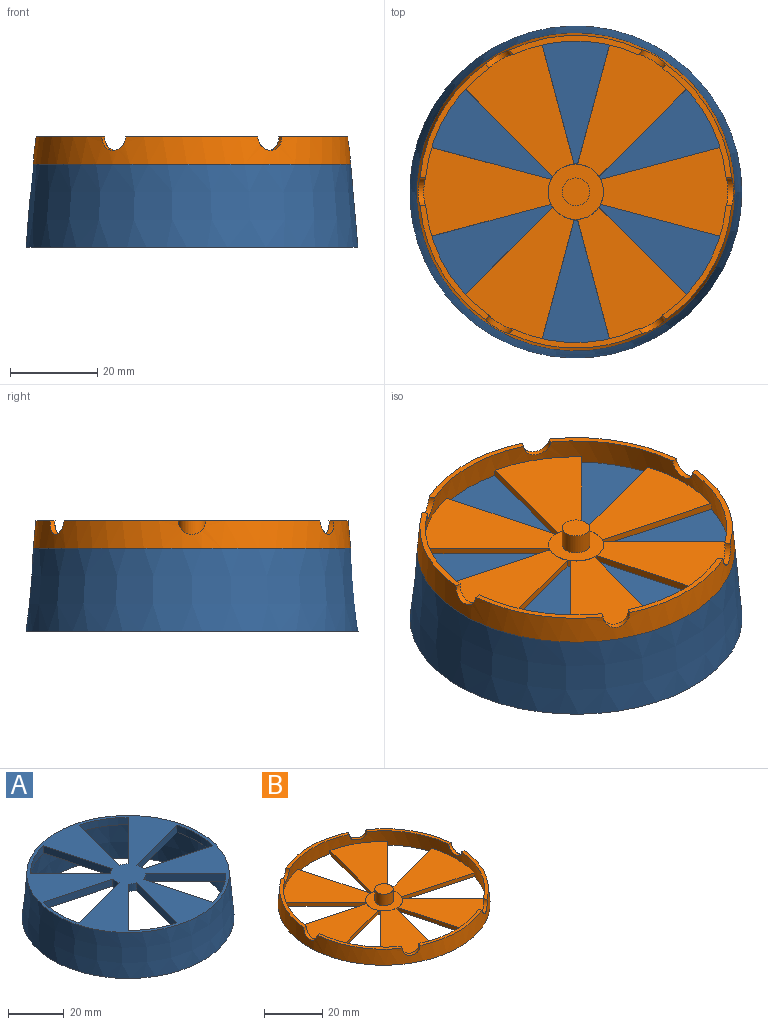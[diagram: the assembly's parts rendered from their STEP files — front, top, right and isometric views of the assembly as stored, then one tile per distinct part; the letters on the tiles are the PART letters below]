
ASSEMBLY  parts=2 mates=1
PART A: 29 faces, bbox 76.2x76.2x19.1 mm
  f0: cone r=38.1mm half-angle=5deg, axis (0,0,-1), area 4477.7mm2, adj f1,f4
  f1: plane 72.87x72.87mm, normal (0,0,1), area 2291.8mm2, adj f0,f5,f6,f7,f8,f9,f10,f11
  f2: plane 70.87x70.87mm, normal (0,0,-1), area 2066.6mm2, adj f3,f5,f6,f7,f8,f9,f10,f11
  f3: cone r=36.83mm half-angle=5deg, axis (0,0,-1), area 3617.6mm2, adj f2,f4
  f4: plane 76.2x76.2mm, normal (0,0,-1), area 300.1mm2, adj f0,f3
  f5: cylinder r=6.35mm len=3.29mm, axis (0,0,1), area 10.6mm2, adj f1,f2,f6,f8
  f6: plane 27.83x7.46mm, normal (-0.26,-0.97,0), area 91.5mm2, adj f1,f2,f5,f7
  f7: cylinder r=35.16mm len=18.2mm, axis (0,0,1), area 58.4mm2, adj f1,f2,f6,f8
  f8: plane 27.83x7.46mm, normal (-0.26,0.97,0), area 91.5mm2, adj f1,f2,f5,f7
  f9: cylinder r=6.35mm len=3.18mm, axis (0,0,1), area 10.6mm2, adj f1,f2,f10,f11
  f10: plane 20.37x20.37mm, normal (0.71,-0.71,0), area 91.5mm2, adj f1,f2,f9,f12
  f11: plane 27.83x7.46mm, normal (-0.97,0.26,0), area 91.5mm2, adj f1,f2,f9,f12
  f12: cylinder r=35.16mm len=15.76mm, axis (0,0,1), area 58.4mm2, adj f1,f2,f10,f11
  f13: cylinder r=6.35mm len=3.18mm, axis (0,0,1), area 10.6mm2, adj f1,f2,f14,f16
  f14: plane 27.83x7.46mm, normal (0.97,0.26,0), area 91.5mm2, adj f1,f2,f13,f15
  f15: cylinder r=35.16mm len=15.76mm, axis (0,0,1), area 58.4mm2, adj f1,f2,f14,f16
  f16: plane 20.37x20.37mm, normal (-0.71,-0.71,0), area 91.5mm2, adj f1,f2,f13,f15
  f17: cylinder r=6.35mm len=3.29mm, axis (0,0,1), area 10.6mm2, adj f1,f2,f18,f19
  f18: plane 27.83x7.46mm, normal (0.26,0.97,0), area 91.5mm2, adj f1,f2,f17,f20
  f19: plane 27.83x7.46mm, normal (0.26,-0.97,0), area 91.5mm2, adj f1,f2,f17,f20
  f20: cylinder r=35.16mm len=18.2mm, axis (0,0,1), area 58.4mm2, adj f1,f2,f18,f19
  f21: cylinder r=6.35mm len=3.18mm, axis (0,0,1), area 10.6mm2, adj f1,f2,f22,f23
  f22: plane 20.37x20.37mm, normal (-0.71,0.71,0), area 91.5mm2, adj f1,f2,f21,f24
  f23: plane 27.83x7.46mm, normal (0.97,-0.26,0), area 91.5mm2, adj f1,f2,f21,f24
  f24: cylinder r=35.16mm len=15.76mm, axis (0,0,1), area 58.4mm2, adj f1,f2,f22,f23
  f25: cylinder r=6.35mm len=3.18mm, axis (0,0,1), area 10.6mm2, adj f1,f2,f26,f27
  f26: plane 27.83x7.46mm, normal (-0.97,-0.26,0), area 91.5mm2, adj f1,f2,f25,f28
  f27: plane 20.37x20.37mm, normal (0.71,0.71,0), area 91.5mm2, adj f1,f2,f25,f28
  f28: cylinder r=35.16mm len=15.76mm, axis (0,0,1), area 58.4mm2, adj f1,f2,f26,f27
PART B: 43 faces, bbox 72.9x72.9x6.4 mm
  f0: cylinder r=3.17mm len=6.35mm, axis (0,0,1), area 95mm2, adj f8,f28
  f1: plane 30.63x25.26mm, normal (0,0,1), area 383.4mm2, adj f25,f26,f27,f42
  f2: plane 30.63x25.26mm, normal (0,0,1), area 383.4mm2, adj f22,f23,f24,f42
  f3: plane 29.34x20.57mm, normal (0,0,1), area 383.4mm2, adj f19,f20,f21,f42
  f4: plane 30.63x25.26mm, normal (0,0,1), area 383.4mm2, adj f16,f17,f18,f42
  f5: plane 30.63x25.26mm, normal (0,0,1), area 383.4mm2, adj f13,f14,f15,f42
  f6: plane 29.34x20.57mm, normal (0,0,1), area 383.4mm2, adj f10,f11,f12,f42
  f7: cone r=6.69mm half-angle=5deg, axis (0,0,-1), area 13.5mm2, adj f8,f9,f10,f11,f12,f13,f14,f15
  f8: plane 12.67x12.67mm, normal (0,0,1), area 94.4mm2, adj f0,f7
  f9: plane 72.87x72.87mm, normal (0,0,-1), area 2731.9mm2, adj f7,f11,f12,f14,f15,f17,f18,f20
  f10: cylinder r=6.35mm len=5.67mm, axis (0,0,-1), area 1mm2, adj f6,f7,f11,f12
  f11: plane 27.93x7.48mm, normal (0.26,0.97,0), area 45.7mm2, adj f6,f7,f9,f10,f42
  f12: plane 27.93x7.48mm, normal (0.26,-0.97,0), area 45.7mm2, adj f6,f7,f9,f10,f42
  f13: cylinder r=6.35mm len=4.91mm, axis (0,0,-1), area 1mm2, adj f5,f7,f14,f15
  f14: plane 20.45x20.45mm, normal (-0.71,0.71,0), area 45.7mm2, adj f5,f7,f9,f13,f42
  f15: plane 27.93x7.48mm, normal (0.97,-0.26,0), area 45.7mm2, adj f5,f7,f9,f13,f42
  f16: cylinder r=6.35mm len=4.91mm, axis (0,0,-1), area 1mm2, adj f4,f7,f17,f18
  f17: plane 27.93x7.48mm, normal (-0.97,-0.26,0), area 45.7mm2, adj f4,f7,f9,f16,f42
  f18: plane 20.45x20.45mm, normal (0.71,0.71,0), area 45.7mm2, adj f4,f7,f9,f16,f42
  f19: cylinder r=6.35mm len=5.67mm, axis (0,0,-1), area 1mm2, adj f3,f7,f20,f21
  f20: plane 27.93x7.48mm, normal (-0.26,-0.97,0), area 45.7mm2, adj f3,f7,f9,f19,f42
  f21: plane 27.93x7.48mm, normal (-0.26,0.97,0), area 45.7mm2, adj f3,f7,f9,f19,f42
  f22: cylinder r=6.35mm len=4.91mm, axis (0,0,-1), area 1mm2, adj f2,f7,f23,f24
  f23: plane 20.45x20.45mm, normal (0.71,-0.71,0), area 45.7mm2, adj f2,f7,f9,f22,f42
  f24: plane 27.93x7.48mm, normal (-0.97,0.26,0), area 45.7mm2, adj f2,f7,f9,f22,f42
  f25: cylinder r=6.35mm len=4.91mm, axis (0,0,-1), area 1mm2, adj f1,f7,f26,f27
  f26: plane 27.93x7.48mm, normal (0.97,0.26,0), area 45.7mm2, adj f1,f7,f9,f25,f42
  f27: plane 20.45x20.45mm, normal (-0.71,-0.71,0), area 45.7mm2, adj f1,f7,f9,f25,f42
  f28: plane 6.35x6.35mm, normal (0,0,1), area 31.7mm2, adj f0
  f29: cylinder r=3.17mm len=6.34mm, axis (0.5,0.87,0), area 12.7mm2, adj f30,f40,f41,f42
  f30: plane 26.19x15.76mm, normal (0,0,1), area 39mm2, adj f29,f31,f40,f42
  f31: cylinder r=3.17mm len=6.34mm, axis (1,0,0), area 12.7mm2, adj f30,f32,f40,f42
  f32: plane 26.19x15.76mm, normal (0,0,1), area 39mm2, adj f31,f33,f40,f42
  f33: cylinder r=3.17mm len=6.34mm, axis (0.5,-0.87,0), area 12.7mm2, adj f32,f34,f40,f42
  f34: plane 30.25x4.45mm, normal (0,0,1), area 39mm2, adj f33,f35,f40,f42
  f35: cylinder r=3.17mm len=6.34mm, axis (-0.5,-0.87,0), area 12.7mm2, adj f34,f36,f40,f42
  f36: plane 26.19x15.76mm, normal (0,0,1), area 39mm2, adj f35,f37,f40,f42
  f37: cylinder r=3.17mm len=6.34mm, axis (-1,0,0), area 12.7mm2, adj f36,f38,f40,f42
  f38: plane 26.19x15.76mm, normal (0,0,1), area 39mm2, adj f37,f39,f40,f42
  f39: cylinder r=3.17mm len=6.34mm, axis (-0.5,0.87,0), area 12.7mm2, adj f38,f40,f41,f42
  f40: cone r=38.1mm half-angle=5deg, axis (0,0,-1), area 1352.8mm2, adj f9,f29,f30,f31,f32,f33,f34,f35
  f41: plane 30.25x4.45mm, normal (0,0,1), area 39mm2, adj f29,f39,f40,f42
  f42: cone r=36.83mm half-angle=5deg, axis (0,0,-1), area 1102mm2, adj f1,f2,f3,f4,f5,f6,f9,f11
PLACE A at identity fixed
PLACE B rot(axis=(0,-0.01,-1),0deg) t=(0,0,0)mm
MATE revolute A.f0 <-> B.f7  axis (0,0,1) through (0,0,69.85)mm
